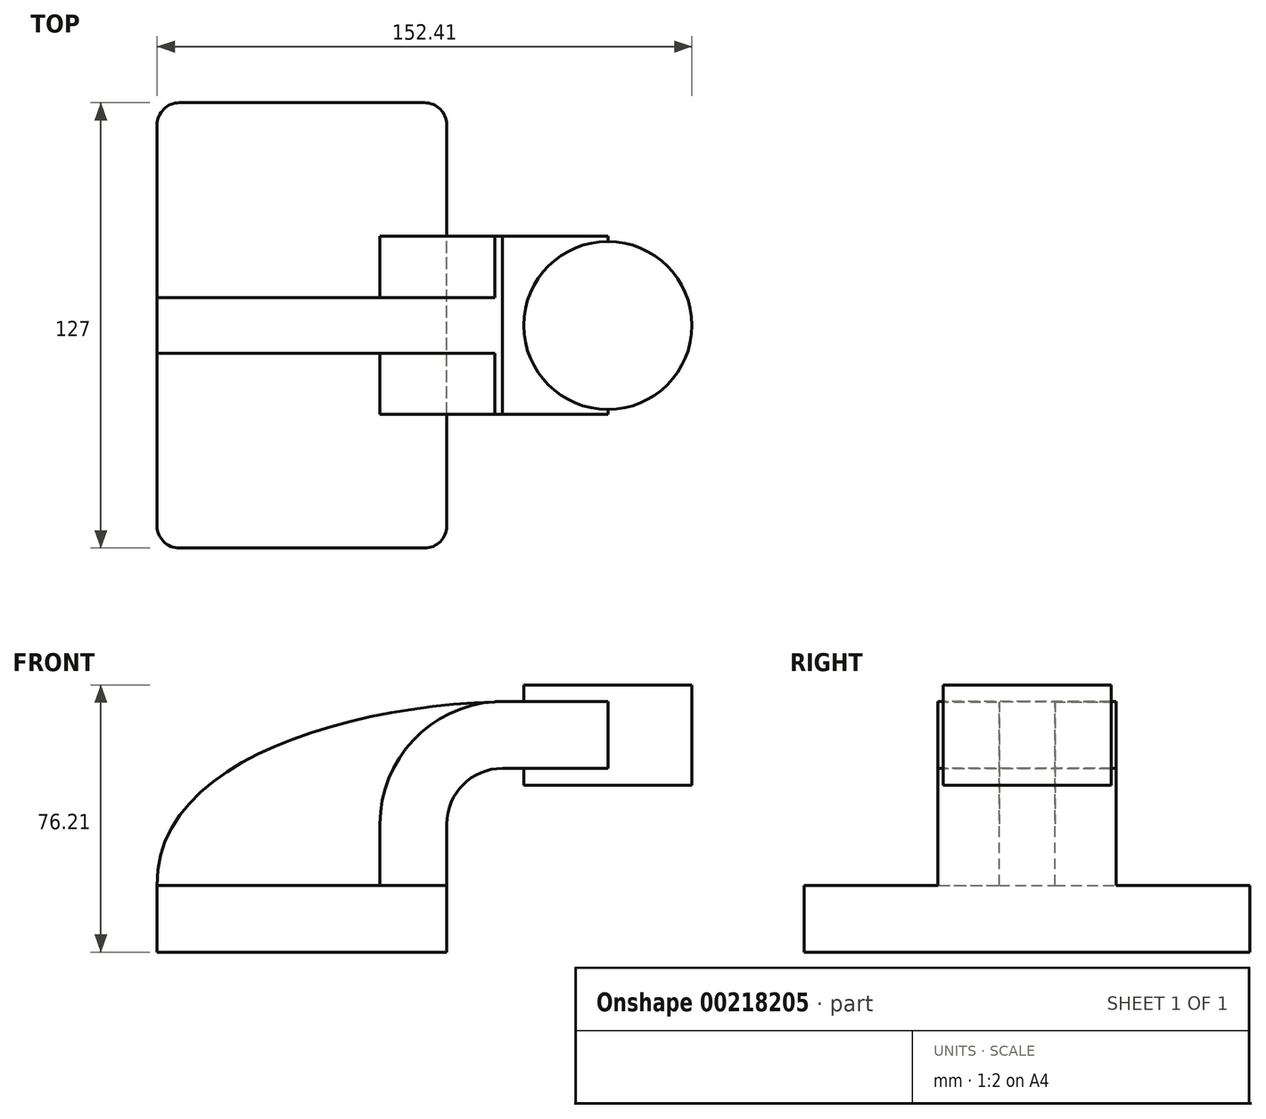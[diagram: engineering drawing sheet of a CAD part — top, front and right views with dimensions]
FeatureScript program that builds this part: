
annotation { "Feature Type Name" : "Feature", "Feature Type Description" : "" }
export const myFeature = defineFeature(function(context is Context, id is Id, definition is map)
    precondition{}
    {
        {
            var Q0;
            Q0=qCreatedBy(makeId("Front.planeOp"),FACE);
            var sketch = newSketch(context, id + "F0", { "sketchPlane" : qUnion([Q0])});
            skLineSegment(sketch, "E0.bottom", {"start": v(-41.28, -9.53) * mm, "end": v(41.28, -9.53) * mm});
            skLineSegment(sketch, "E0.top", {"start": v(-41.28, 9.52) * mm, "end": v(41.28, 9.52) * mm});
            skLineSegment(sketch, "E0.left", {"start": v(-41.28, -9.53) * mm, "end": v(-41.28, 9.53) * mm});
            skLineSegment(sketch, "E0.right", {"start": v(41.28, -9.53) * mm, "end": v(41.28, 9.52) * mm});
            skPoint(sketch, "E0.middle", {"position": v(0, 0) * mm});
            skLineSegment(sketch, "E1.bottom", {"start": v(60.33, 38.1) * mm, "end": v(111.12, 38.1) * mm});
            skLineSegment(sketch, "E1.top", {"start": v(60.33, 66.67) * mm, "end": v(111.12, 66.67) * mm});
            skLineSegment(sketch, "E1.left", {"start": v(60.33, 38.1) * mm, "end": v(60.32, 66.67) * mm});
            skLineSegment(sketch, "E1.right", {"start": v(111.12, 38.1) * mm, "end": v(111.12, 66.67) * mm});
            skPoint(sketch, "E1.middle", {"position": v(85.72, 52.39) * mm});
            skLineSegment(sketch, "E2", {"start": v(41.27, 9.52) * mm, "end": v(41.27, 27) * mm});
            skArc(sketch, "E3", {"start": v(41.27, 27) * mm, "mid": v(45.92, 38.23) * mm, "end": v(57.15, 42.88) * mm});
            skLineSegment(sketch, "E4", {"start": v(57.15, 42.88) * mm, "end": v(87.16, 42.88) * mm});
            skLineSegment(sketch, "E5.0", {"start": v(57.15, 61.93) * mm, "end": v(87.16, 61.93) * mm});
            skArc(sketch, "E5.1", {"start": v(22.23, 27) * mm, "mid": v(32.45, 51.7) * mm, "end": v(57.15, 61.93) * mm});
            skLineSegment(sketch, "E5.2", {"start": v(22.22, 9.52) * mm, "end": v(22.22, 27) * mm});
            skLineSegment(sketch, "E6", {"start": v(87.16, 38.1) * mm, "end": v(87.16, 66.67) * mm});
            skPoint(sketch, "E6.startSnap0", {"position": v(85.72, 38.1) * mm});
            skFitSpline(sketch, "E7", {"points": [v(-41.28, 9.53) * mm, v(57.15, 61.93) * mm], "startDerivative": vector(-1.98, 105.42) * mm, "endDerivative": vector(136.12, 3.53) * mm});
            skSolve(sketch);
        }
        {
            var Q0;
            Q0=makeQuery(id+"F0.imprint","IMPRINT",FACE,{"disambiguationData":[TD([[makeQuery(id+"F0.imprint","IMPRINT",EDGE,{"derivedFrom":sQuery(id+"F0.wireOp",EDGE,"E0.bottom")}),1.0]])]});
            extrude(context, id + "F1", {"entities" : qUnion([Q0]), "endBound" : BoundingType.SYMMETRIC, "depth" : 127 * mm});
        }
        {
            var Q0;
            {var subQ1=sQuery(id+"F0.wireOp",EDGE,"E2");Q0=makeQuery(id+"F0.imprint","IMPRINT",FACE,{"disambiguationData":[TD([[makeQuery(id+"F0.imprint","IMPRINT",EDGE,{"derivedFrom":subQ1}),1.0]])]});}
            var Q1;
            {var subQ0=sQuery(id+"F0.wireOp",EDGE,"E4");var subQ1=sQuery(id+"F0.wireOp",EDGE,"E1.left");var subQ2=makeQuery(id+"F0.imprint","INTERSECT",VERTEX,{"derivedFrom":[subQ1,subQ0]});Q1=makeQuery(id+"F0.imprint","IMPRINT",FACE,{"disambiguationData":[TD([[makeQuery(id+"F0.imprint","IMPRINT",EDGE,{"disambiguationData":[TD([[subQ2,-1.0]])],"derivedFrom":subQ1}),-1.0]])]});}
            extrude(context, id + "F2", {"entities" : qUnion([Q0, Q1]), "operationType" : NewBodyOperationType.ADD, "endBound" : BoundingType.SYMMETRIC, "depth" : 50.8 * mm});
        }
        {
            var Q0;
            {var subQ3=sQuery(id+"F0.wireOp",EDGE,"E5.2");Q0=makeQuery(id+"F0.imprint","IMPRINT",FACE,{"disambiguationData":[TD([[makeQuery(id+"F0.imprint","IMPRINT",EDGE,{"derivedFrom":subQ3}),1.0]])]});}
            extrude(context, id + "F3", {"entities" : qUnion([Q0]), "operationType" : NewBodyOperationType.ADD, "endBound" : BoundingType.SYMMETRIC, "depth" : 15.88 * mm});
        }
        {
            var Q0;
            {var subQ0=sQuery(id+"F0.wireOp",EDGE,"E1.right");Q0=makeQuery(id+"F0.imprint","IMPRINT",FACE,{"disambiguationData":[TD([[makeQuery(id+"F0.imprint","IMPRINT",EDGE,{"derivedFrom":subQ0}),1.0]])]});}
            var Q1;
            Q1=sQuery(id+"F0.wireOp",EDGE,"E6");
            revolve(context, id + "F4", {"operationType" : NewBodyOperationType.ADD, "entities" : qUnion([Q0]), "axis" : qUnion([Q1]), "revolveType" : RevolveType.FULL});
        }
        {
            var Q0;
            Q0=makeQuery(id+"F1.opExtrude","CAP_EDGE",EDGE,{"disambiguationData":[OSD([sQuery(id+"F0.wireOp",EDGE,"E0.left")])],"isStart":false});
            var Q1;
            Q1=makeQuery(id+"F1.opExtrude","CAP_EDGE",EDGE,{"disambiguationData":[OSD([sQuery(id+"F0.wireOp",EDGE,"E0.right")])],"isStart":false});
            var Q2;
            Q2=makeQuery(id+"F1.opExtrude","CAP_EDGE",EDGE,{"disambiguationData":[OSD([sQuery(id+"F0.wireOp",EDGE,"E0.right")])],"isStart":true});
            var Q3;
            Q3=makeQuery(id+"F1.opExtrude","CAP_EDGE",EDGE,{"disambiguationData":[OSD([sQuery(id+"F0.wireOp",EDGE,"E0.left")])],"isStart":true});
            fillet(context, id + "F5", {"entities" : qUnion([Q0, Q1, Q2, Q3]), "radius" : 6.35 * mm, "tangentPropagation" : true, "allowEdgeOverflow" : false});
        }
    });
